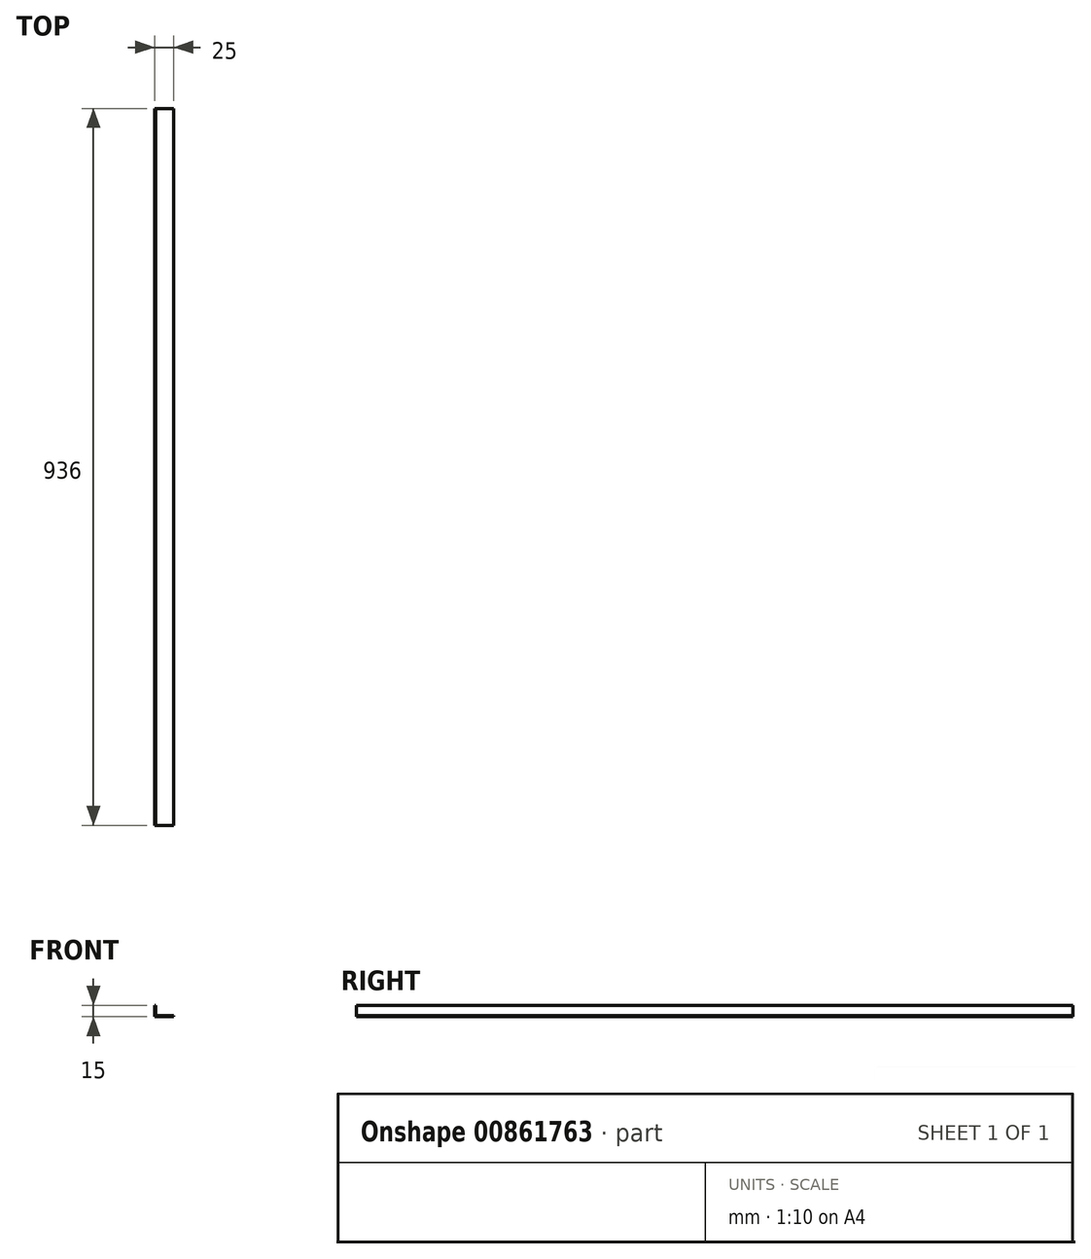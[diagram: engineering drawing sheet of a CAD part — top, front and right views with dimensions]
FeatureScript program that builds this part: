
annotation { "Feature Type Name" : "Feature", "Feature Type Description" : "" }
export const myFeature = defineFeature(function(context is Context, id is Id, definition is map)
    precondition{}
    {
        {
            var Q0;
            Q0=qCreatedBy(makeId("Front.planeOp"),FACE);
            var sketch = newSketch(context, id + "F0", { "sketchPlane" : qUnion([Q0])});
            skLineSegment(sketch, "E0", {"start": v(-21.04, 13.9) * mm, "end": v(-21.04, -1.1) * mm});
            skLineSegment(sketch, "E1", {"start": v(-21.04, -1.1) * mm, "end": v(3.96, -1.1) * mm});
            skLineSegment(sketch, "E2", {"start": v(3.96, -1.1) * mm, "end": v(3.96, 0.5) * mm});
            skLineSegment(sketch, "E3", {"start": v(3.96, 0.5) * mm, "end": v(-19.44, 0.5) * mm});
            skLineSegment(sketch, "E4", {"start": v(-19.44, 0.5) * mm, "end": v(-19.44, 13.87) * mm});
            skLineSegment(sketch, "E5", {"start": v(-19.44, 13.87) * mm, "end": v(-21.04, 13.9) * mm});
            skSolve(sketch);
        }
        {
            var Q0;
            Q0=makeQuery(id+"F0.imprint","IMPRINT",FACE,{"disambiguationData":[TD([[makeQuery(id+"F0.imprint","IMPRINT",EDGE,{"derivedFrom":sQuery(id+"F0.wireOp",EDGE,"E0")}),1.0]])]});
            extrude(context, id + "F1", {"entities" : qUnion([Q0]), "endBound" : BoundingType.SYMMETRIC, "oppositeDirection" : true, "depth" : 936 * mm, "offsetDistance" : 25 * mm});
        }
    });
